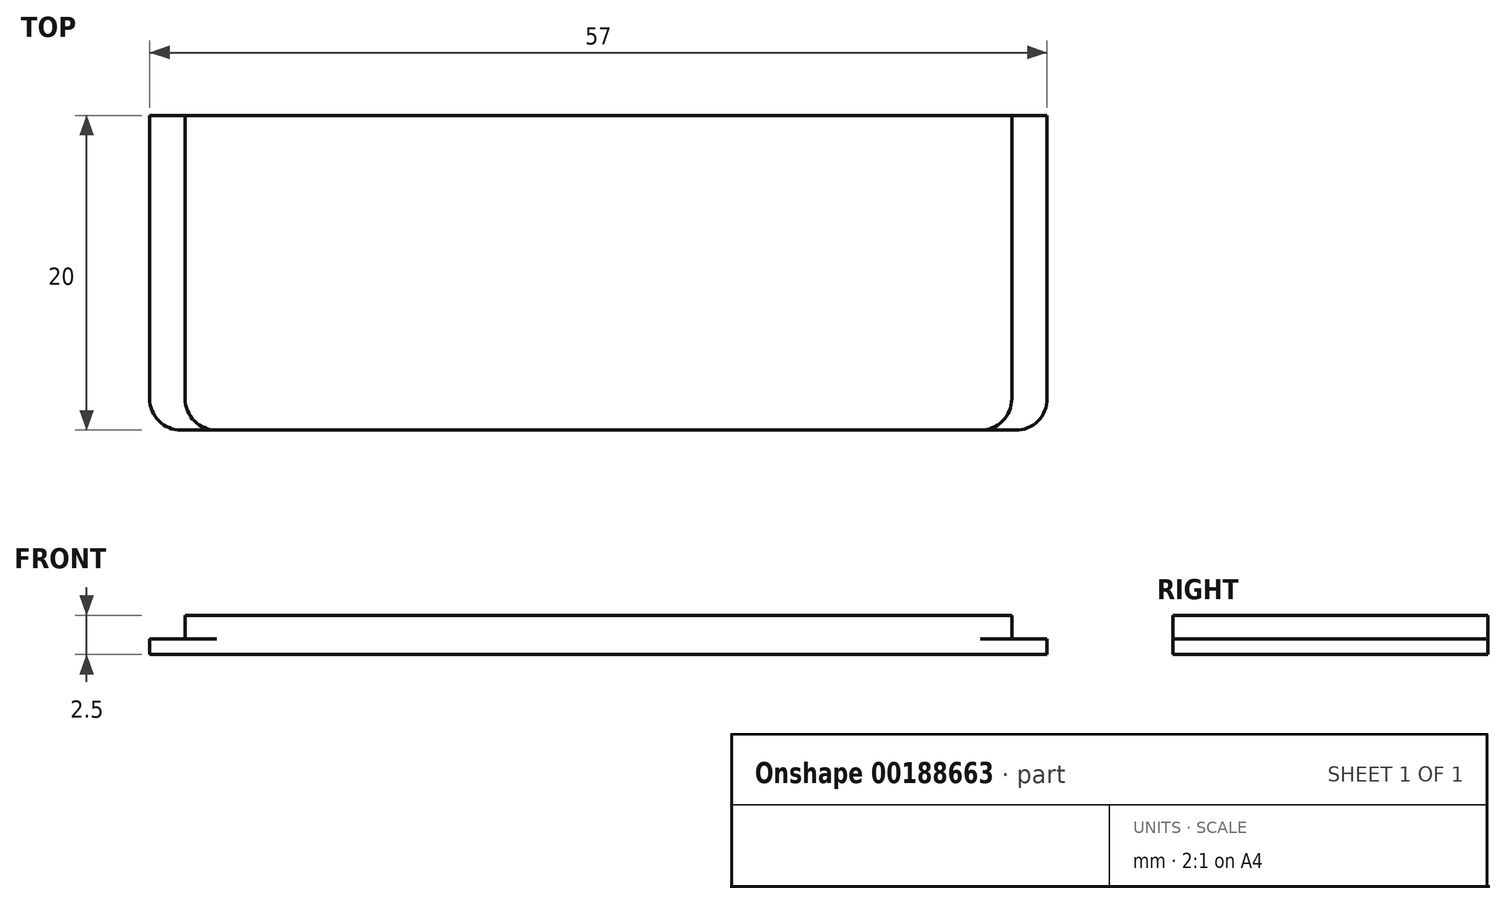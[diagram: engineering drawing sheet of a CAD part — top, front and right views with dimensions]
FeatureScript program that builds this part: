
annotation { "Feature Type Name" : "Feature", "Feature Type Description" : "" }
export const myFeature = defineFeature(function(context is Context, id is Id, definition is map)
    precondition{}
    {
        {
            var Q0;
            Q0=qCreatedBy(makeId("Top.planeOp"),FACE);
            var sketch = newSketch(context, id + "F0", { "sketchPlane" : qUnion([Q0])});
            skLineSegment(sketch, "E0.bottom", {"start": v(2, 0) * mm, "end": v(55, 0) * mm});
            skLineSegment(sketch, "E0.top", {"start": v(0, 20) * mm, "end": v(57, 20) * mm});
            skLineSegment(sketch, "E0.left", {"start": v(0, 2) * mm, "end": v(0, 20) * mm});
            skLineSegment(sketch, "E0.right", {"start": v(57, 2) * mm, "end": v(57, 20) * mm});
            skPoint(sketch, "E1.visualSharp", {"position": v(0, 0) * mm});
            skArc(sketch, "E1.filletArc", {"start": v(0, 2) * mm, "mid": v(0.59, 0.59) * mm, "end": v(2, 0) * mm});
            skPoint(sketch, "E2.visualSharp", {"position": v(57, 0) * mm});
            skArc(sketch, "E2.filletArc", {"start": v(55, 0) * mm, "mid": v(56.41, 0.59) * mm, "end": v(57, 2) * mm});
            skSolve(sketch);
        }
        {
            var Q0;
            Q0=qSketchRegion(id+"F0",true);
            extrude(context, id + "F1", {"entities" : qUnion([Q0]), "depth" : 1 * mm});
        }
        {
            var Q0;
            Q0=makeQuery(id+"F1.opExtrude","CAP_FACE",FACE,{"disambiguationData":[OSD([sQuery(id+"F0.wireOp",EDGE,"E0.bottom"),sQuery(id+"F0.wireOp",EDGE,"E0.top"),sQuery(id+"F0.wireOp",EDGE,"E0.left"),sQuery(id+"F0.wireOp",EDGE,"E0.right")])],"isStart":false});
            var sketch = newSketch(context, id + "F2", { "sketchPlane" : qUnion([Q0])});
            skLineSegment(sketch, "E3", {"start": v(2.25, 20) * mm, "end": v(54.75, 20) * mm});
            skLineSegment(sketch, "E4", {"start": v(54.75, 20) * mm, "end": v(54.75, 2) * mm});
            skLineSegment(sketch, "E5", {"start": v(52.75, 0) * mm, "end": v(4.25, 0) * mm});
            skLineSegment(sketch, "E6", {"start": v(2.25, 2) * mm, "end": v(2.25, 20) * mm});
            skPoint(sketch, "E7", {"position": v(28.5, 20) * mm});
            skPoint(sketch, "E8.visualSharp", {"position": v(2.25, 0) * mm});
            skArc(sketch, "E8.filletArc", {"start": v(2.25, 2) * mm, "mid": v(2.84, 0.59) * mm, "end": v(4.25, 0) * mm});
            skPoint(sketch, "E9.visualSharp", {"position": v(54.75, 0) * mm});
            skArc(sketch, "E9.filletArc", {"start": v(52.75, 0) * mm, "mid": v(54.16, 0.59) * mm, "end": v(54.75, 2) * mm});
            skSolve(sketch);
        }
        {
            var Q0;
            Q0=qSketchRegion(id+"F2",true);
            extrude(context, id + "F3", {"entities" : qUnion([Q0]), "operationType" : NewBodyOperationType.ADD, "depth" : 1.5 * mm});
        }
    });
